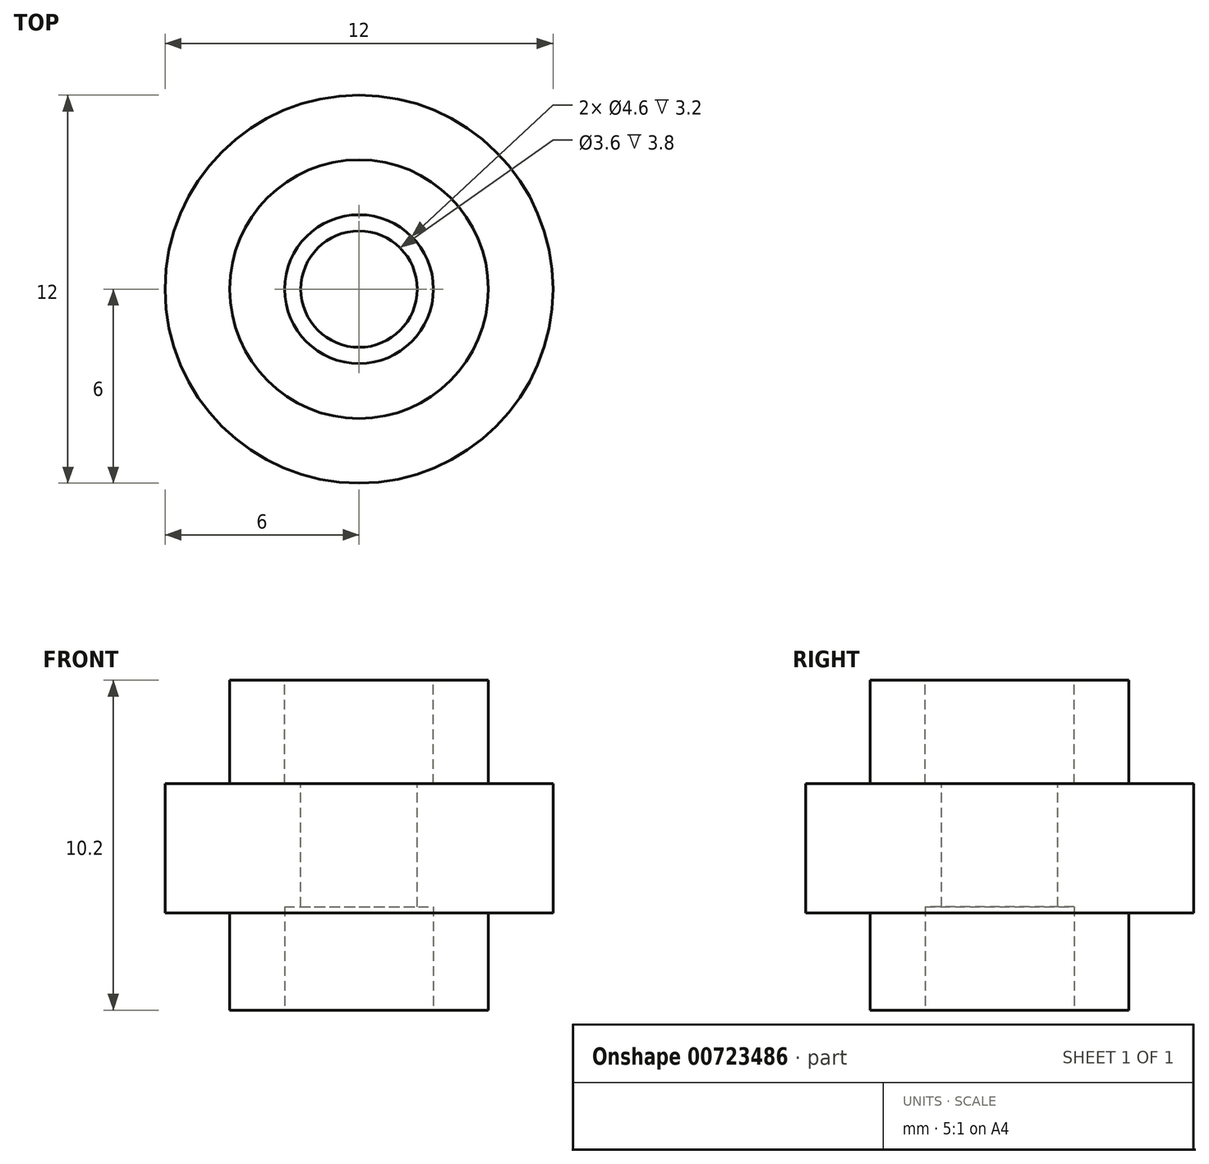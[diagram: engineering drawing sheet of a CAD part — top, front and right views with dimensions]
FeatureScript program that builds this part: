
annotation { "Feature Type Name" : "Feature", "Feature Type Description" : "" }
export const myFeature = defineFeature(function(context is Context, id is Id, definition is map)
    precondition{}
    {
        {
            var Q0;
            Q0=qCreatedBy(makeId("Top.planeOp"),FACE);
            var sketch = newSketch(context, id + "F0", { "sketchPlane" : qUnion([Q0])});
            skCircle(sketch, "E0", {"center": v(0, 0) * mm, "radius": 4 * mm});
            skSolve(sketch);
        }
        {
            var Q0;
            Q0 = qSketchRegion(id + "F0", true);
            extrude(context, id + "F1", {"entities" : qUnion([Q0]), "depth" : 3 * mm, "offsetDistance" : 25 * mm});
        }
        {
            var Q0;
            Q0=makeQuery(id+"F1.opExtrude","CAP_FACE",FACE,{"disambiguationData":[OSD([sQuery(id+"F0.wireOp",EDGE,"E0")])],"isStart":false});
            var sketch = newSketch(context, id + "F2", { "sketchPlane" : qUnion([Q0])});
            skCircle(sketch, "E1", {"center": v(0, 0) * mm, "radius": 6 * mm});
            skSolve(sketch);
        }
        {
            var Q0;
            Q0 = qSketchRegion(id + "F2", true);
            extrude(context, id + "F3", {"entities" : qUnion([Q0]), "operationType" : NewBodyOperationType.ADD, "depth" : 4 * mm, "offsetDistance" : 25 * mm});
        }
        {
            var Q0;
            Q0=makeQuery(id+"F3.opExtrude","CAP_FACE",FACE,{"disambiguationData":[OSD([sQuery(id+"F2.wireOp",EDGE,"E1")])],"isStart":false});
            var sketch = newSketch(context, id + "F4", { "sketchPlane" : qUnion([Q0])});
            skCircle(sketch, "E2", {"center": v(0, 0) * mm, "radius": 4 * mm});
            skSolve(sketch);
        }
        {
            var Q0;
            Q0 = qSketchRegion(id + "F4", true);
            extrude(context, id + "F5", {"entities" : qUnion([Q0]), "operationType" : NewBodyOperationType.ADD, "depth" : 3.2 * mm, "offsetDistance" : 25 * mm});
        }
        {
            var Q0;
            Q0=makeQuery(id+"F5.opExtrude","CAP_FACE",FACE,{"disambiguationData":[OSD([sQuery(id+"F4.wireOp",EDGE,"E2")])],"isStart":false});
            var sketch = newSketch(context, id + "F6", { "sketchPlane" : qUnion([Q0])});
            skCircle(sketch, "E3", {"center": v(0, 0) * mm, "radius": 1.8 * mm});
            skSolve(sketch);
        }
        {
            var Q0;
            Q0 = qSketchRegion(id + "F6", true);
            extrude(context, id + "F7", {"entities" : qUnion([Q0]), "operationType" : NewBodyOperationType.REMOVE, "endBound" : BoundingType.THROUGH_ALL, "oppositeDirection" : true, "depth" : 25 * mm, "offsetDistance" : 25 * mm});
        }
        {
            var Q0;
            Q0=makeQuery(id+"F5.opExtrude","CAP_FACE",FACE,{"disambiguationData":[OSD([sQuery(id+"F4.wireOp",EDGE,"E2")])],"isStart":false});
            var sketch = newSketch(context, id + "F8", { "sketchPlane" : qUnion([Q0])});
            skCircle(sketch, "E4", {"center": v(0, 0) * mm, "radius": 2.3 * mm});
            skSolve(sketch);
        }
        {
            var Q0;
            Q0 = qSketchRegion(id + "F8", true);
            extrude(context, id + "F9", {"entities" : qUnion([Q0]), "operationType" : NewBodyOperationType.REMOVE, "oppositeDirection" : true, "depth" : 3.2 * mm, "offsetDistance" : 25 * mm});
        }
        {
            var Q0;
            Q0=makeQuery(id+"F1.opExtrude","CAP_FACE",FACE,{"disambiguationData":[OSD([sQuery(id+"F0.wireOp",EDGE,"E0")])],"isStart":true});
            var sketch = newSketch(context, id + "F10", { "sketchPlane" : qUnion([Q0])});
            skCircle(sketch, "E5", {"center": v(0, 0) * mm, "radius": 2.3 * mm});
            skSolve(sketch);
        }
        {
            var Q0;
            Q0 = qSketchRegion(id + "F10", true);
            extrude(context, id + "F11", {"entities" : qUnion([Q0]), "operationType" : NewBodyOperationType.REMOVE, "oppositeDirection" : true, "depth" : 3.2 * mm, "offsetDistance" : 25 * mm});
        }
    });
